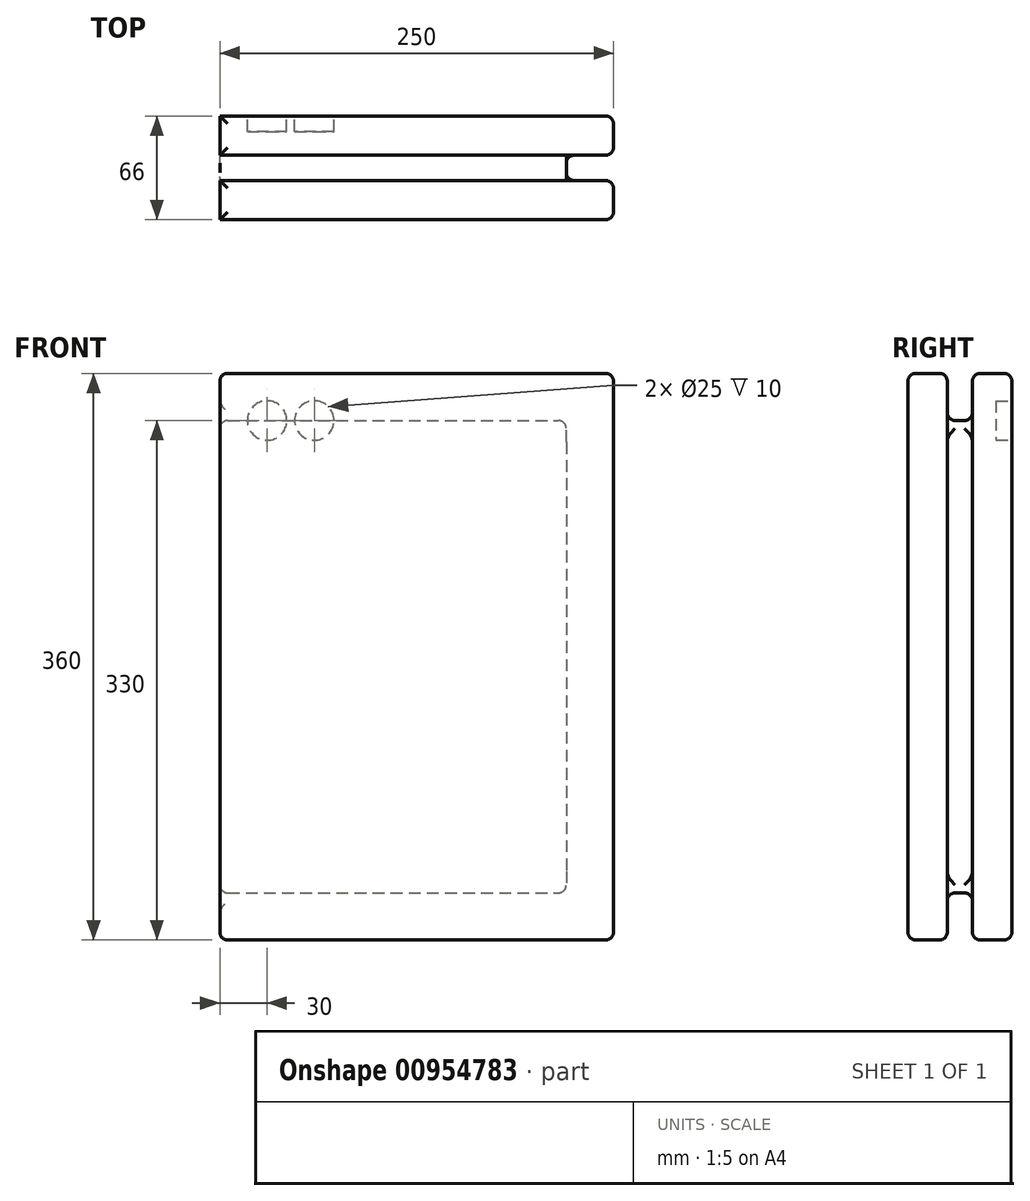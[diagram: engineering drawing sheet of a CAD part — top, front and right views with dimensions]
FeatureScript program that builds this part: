
annotation { "Feature Type Name" : "Feature", "Feature Type Description" : "" }
export const myFeature = defineFeature(function(context is Context, id is Id, definition is map)
    precondition{}
    {
        {
            var Q0;
            Q0=qCreatedBy(makeId("Right.planeOp"),FACE);
            var sketch = newSketch(context, id + "F0", { "sketchPlane" : qUnion([Q0])});
            skLineSegment(sketch, "E0", {"start": v(0, 0) * mm, "end": v(0, 150) * mm, "construction": true});
            skLineSegment(sketch, "E1", {"start": v(0, 0) * mm, "end": v(0, -150) * mm, "construction": true});
            skLineSegment(sketch, "E2", {"start": v(0, 150) * mm, "end": v(8, 150) * mm});
            skLineSegment(sketch, "E3", {"start": v(8, 150) * mm, "end": v(8, 180) * mm});
            skLineSegment(sketch, "E4", {"start": v(8, 180) * mm, "end": v(33, 180) * mm});
            skLineSegment(sketch, "E5", {"start": v(0, 0) * mm, "end": v(80, 0) * mm, "construction": true});
            skLineSegment(sketch, "E6", {"start": v(0, 0) * mm, "end": v(-80, 0) * mm, "construction": true});
            skLineSegment(sketch, "E7.MirrorCS", {"start": v(8, -180) * mm, "end": v(33, -180) * mm});
            skLineSegment(sketch, "E8.MirrorCS", {"start": v(8, -150) * mm, "end": v(8, -180) * mm});
            skLineSegment(sketch, "E9.MirrorCS", {"start": v(0, -150) * mm, "end": v(8, -150) * mm});
            skLineSegment(sketch, "E10", {"start": v(33, 180) * mm, "end": v(33, -180) * mm});
            skLineSegment(sketch, "E11", {"start": v(0, 150) * mm, "end": v(0, -150) * mm, "construction": true});
            skLineSegment(sketch, "E12.MirrorCS", {"start": v(0, 150) * mm, "end": v(-8, 150) * mm});
            skLineSegment(sketch, "E13.MirrorCS", {"start": v(-8, 150) * mm, "end": v(-8, 180) * mm});
            skLineSegment(sketch, "E14.MirrorCS", {"start": v(-8, 180) * mm, "end": v(-33, 180) * mm});
            skLineSegment(sketch, "E15.MirrorCS", {"start": v(-33, 180) * mm, "end": v(-33, -180) * mm});
            skLineSegment(sketch, "E16.MirrorCS", {"start": v(-8, -180) * mm, "end": v(-33, -180) * mm});
            skLineSegment(sketch, "E17.MirrorCS", {"start": v(-8, -150) * mm, "end": v(-8, -180) * mm});
            skLineSegment(sketch, "E18.MirrorCS", {"start": v(0, -150) * mm, "end": v(-8, -150) * mm});
            skSolve(sketch);
        }
        {
            var Q0;
            Q0=qCreatedBy(makeId("Front.planeOp"),FACE);
            var sketch = newSketch(context, id + "F1", { "sketchPlane" : qUnion([Q0])});
            skLineSegment(sketch, "E19", {"start": v(0, 0) * mm, "end": v(250, 0) * mm});
            skSolve(sketch);
        }
        {
            var Q0;
            Q0 = qSketchRegion(id + "F0", true);
            var Q1;
            Q1 = qConstructionFilter(qBodyType(qCreatedBy(id + "F1" ,EDGE), BodyType.WIRE), ConstructionObject.NO);
            sweep(context, id + "F2", {"profiles" : qUnion([Q0]), "path" : qUnion([Q1])});
        }
        {
            var Q0;
            Q0=makeQuery(id+"F2.opSweep","SWEPT_FACE",FACE,{"disambiguationData":[OSD([sQuery(id+"F0.wireOp",EDGE,"E10"),sQuery(id+"F1.wireOp",EDGE,"E19")])]});
            var sketch = newSketch(context, id + "F3", { "sketchPlane" : qUnion([Q0])});
            skLineSegment(sketch, "E20", {"start": v(0, 180) * mm, "end": v(-30, 180) * mm, "construction": true});
            skLineSegment(sketch, "E21", {"start": v(-30, 180) * mm, "end": v(-60, 180) * mm, "construction": true});
            skLineSegment(sketch, "E22", {"start": v(-30, 180) * mm, "end": v(-30, 150) * mm, "construction": true});
            skLineSegment(sketch, "E23", {"start": v(-60, 180) * mm, "end": v(-60, 150) * mm, "construction": true});
            skCircle(sketch, "E24", {"center": v(-30, 150) * mm, "radius": 12.5 * mm});
            skCircle(sketch, "E25", {"center": v(-60, 150) * mm, "radius": 12.5 * mm});
            skSolve(sketch);
        }
        {
            var Q0;
            Q0=makeQuery(id+"F3.imprint","IMPRINT",FACE,{"disambiguationData":[TD([[makeQuery(id+"F3.imprint","IMPRINT",EDGE,{"derivedFrom":sQuery(id+"F3.wireOp",EDGE,"E25")}),1.0]])]});
            var Q1;
            Q1=makeQuery(id+"F3.imprint","IMPRINT",FACE,{"disambiguationData":[TD([[makeQuery(id+"F3.imprint","IMPRINT",EDGE,{"derivedFrom":sQuery(id+"F3.wireOp",EDGE,"E24")}),1.0]])]});
            extrude(context, id + "F4", {"entities" : qUnion([Q0, Q1]), "operationType" : NewBodyOperationType.REMOVE, "oppositeDirection" : true, "depth" : 10 * mm, "offsetDistance" : 25 * mm});
        }
        {
            var Q0;
            Q0=makeQuery(id+"F2.opSweep","CAP_FACE",FACE,{"disambiguationData":[OSD([sQuery(id+"F0.wireOp",EDGE,"E2"),sQuery(id+"F0.wireOp",EDGE,"E3"),sQuery(id+"F0.wireOp",EDGE,"E4"),sQuery(id+"F0.wireOp",EDGE,"E7.MirrorCS"),sQuery(id+"F0.wireOp",EDGE,"E8.MirrorCS"),sQuery(id+"F0.wireOp",EDGE,"E9.MirrorCS"),sQuery(id+"F0.wireOp",EDGE,"E10"),sQuery(id+"F0.wireOp",EDGE,"E12.MirrorCS"),sQuery(id+"F0.wireOp",EDGE,"E13.MirrorCS"),sQuery(id+"F0.wireOp",EDGE,"E14.MirrorCS"),sQuery(id+"F0.wireOp",EDGE,"E15.MirrorCS"),sQuery(id+"F0.wireOp",EDGE,"E16.MirrorCS"),sQuery(id+"F0.wireOp",EDGE,"E17.MirrorCS"),sQuery(id+"F0.wireOp",EDGE,"E18.MirrorCS"),sQuery(id+"F1.wireOp",VERTEX,"E19.end")])],"isStart":false});
            var sketch = newSketch(context, id + "F5", { "sketchPlane" : qUnion([Q0])});
            skPoint(sketch, "E26", {"position": v(0, 0) * mm});
            skLineSegment(sketch, "E27", {"start": v(0, 0) * mm, "end": v(0, 150) * mm, "construction": true});
            skLineSegment(sketch, "E28", {"start": v(0, 0) * mm, "end": v(0, -150) * mm, "construction": true});
            skLineSegment(sketch, "E29", {"start": v(0, 150) * mm, "end": v(-8, 150) * mm});
            skLineSegment(sketch, "E30", {"start": v(-8, 150) * mm, "end": v(-8, -150) * mm});
            skLineSegment(sketch, "E31", {"start": v(-8, -150) * mm, "end": v(0, -150) * mm});
            skLineSegment(sketch, "E32.MirrorCS", {"start": v(0, 150) * mm, "end": v(8, 150) * mm});
            skLineSegment(sketch, "E33.MirrorCS", {"start": v(8, 150) * mm, "end": v(8, -150) * mm});
            skLineSegment(sketch, "E34.MirrorCS", {"start": v(8, -150) * mm, "end": v(0, -150) * mm});
            skSolve(sketch);
        }
        {
            var Q0;
            Q0=makeQuery(id+"F5.imprint","IMPRINT",FACE,{"disambiguationData":[TD([[makeQuery(id+"F5.imprint","IMPRINT",EDGE,{"derivedFrom":sQuery(id+"F5.wireOp",EDGE,"E29")}),1.0]])]});
            extrude(context, id + "F6", {"entities" : qUnion([Q0]), "operationType" : NewBodyOperationType.REMOVE, "oppositeDirection" : true, "depth" : 30 * mm, "offsetDistance" : 25 * mm});
        }
        {
            var Q0;
            Q0=makeQuery(id+"F2.opSweep","SWEPT_FACE",FACE,{"disambiguationData":[OSD([sQuery(id+"F0.wireOp",EDGE,"E2"),sQuery(id+"F0.wireOp",EDGE,"E12.MirrorCS"),sQuery(id+"F1.wireOp",EDGE,"E19")])]});
            var Q1;
            Q1=makeQuery(id+"F2.opSweep","SWEPT_FACE",FACE,{"disambiguationData":[OSD([sQuery(id+"F0.wireOp",EDGE,"E9.MirrorCS"),sQuery(id+"F0.wireOp",EDGE,"E18.MirrorCS"),sQuery(id+"F1.wireOp",EDGE,"E19")])]});
            var Q2;
            Q2=makeQuery(id+"F2.opSweep","SWEPT_FACE",FACE,{"disambiguationData":[OSD([sQuery(id+"F0.wireOp",EDGE,"E7.MirrorCS"),sQuery(id+"F1.wireOp",EDGE,"E19")])]});
            var Q3;
            {var subQ1=sQuery(id+"F0.wireOp",EDGE,"E8.MirrorCS");var subQ2=sQuery(id+"F0.wireOp",EDGE,"E7.MirrorCS");var subQ3=sQuery(id+"F0.wireOp",EDGE,"E4");var subQ4=sQuery(id+"F0.wireOp",EDGE,"E3");var subQ5=sQuery(id+"F0.wireOp",EDGE,"E10");Q3=makeQuery(id+"F6.boolean.opBoolean","SPLIT",FACE,{"disambiguationData":[TD([makeQuery(id+"F6.opExtrude","SWEPT_FACE",FACE,{"disambiguationData":[OSD([sQuery(id+"F5.wireOp",EDGE,"E33.MirrorCS")])]})])],"derivedFrom":makeQuery(id+"F2.opSweep","CAP_FACE",FACE,{"disambiguationData":[OSD([sQuery(id+"F0.wireOp",EDGE,"E2"),subQ4,subQ3,subQ2,subQ1,sQuery(id+"F0.wireOp",EDGE,"E9.MirrorCS"),subQ5,sQuery(id+"F0.wireOp",EDGE,"E12.MirrorCS"),sQuery(id+"F0.wireOp",EDGE,"E13.MirrorCS"),sQuery(id+"F0.wireOp",EDGE,"E14.MirrorCS"),sQuery(id+"F0.wireOp",EDGE,"E15.MirrorCS"),sQuery(id+"F0.wireOp",EDGE,"E16.MirrorCS"),sQuery(id+"F0.wireOp",EDGE,"E17.MirrorCS"),sQuery(id+"F0.wireOp",EDGE,"E18.MirrorCS"),sQuery(id+"F1.wireOp",VERTEX,"E19.end")])],"isStart":false})});}
            var Q4;
            Q4=makeQuery(id+"F2.opSweep","SWEPT_FACE",FACE,{"disambiguationData":[OSD([sQuery(id+"F0.wireOp",EDGE,"E4"),sQuery(id+"F1.wireOp",EDGE,"E19")])]});
            var Q5;
            Q5=makeQuery(id+"F2.opSweep","SWEPT_FACE",FACE,{"disambiguationData":[OSD([sQuery(id+"F0.wireOp",EDGE,"E14.MirrorCS"),sQuery(id+"F1.wireOp",EDGE,"E19")])]});
            var Q6;
            {var subQ1=sQuery(id+"F0.wireOp",EDGE,"E16.MirrorCS");var subQ2=sQuery(id+"F0.wireOp",EDGE,"E15.MirrorCS");var subQ3=sQuery(id+"F0.wireOp",EDGE,"E14.MirrorCS");var subQ4=sQuery(id+"F0.wireOp",EDGE,"E13.MirrorCS");var subQ5=sQuery(id+"F0.wireOp",EDGE,"E17.MirrorCS");Q6=makeQuery(id+"F6.boolean.opBoolean","SPLIT",FACE,{"disambiguationData":[TD([makeQuery(id+"F6.opExtrude","SWEPT_FACE",FACE,{"disambiguationData":[OSD([sQuery(id+"F5.wireOp",EDGE,"E30")])]})])],"derivedFrom":makeQuery(id+"F2.opSweep","CAP_FACE",FACE,{"disambiguationData":[OSD([sQuery(id+"F0.wireOp",EDGE,"E2"),sQuery(id+"F0.wireOp",EDGE,"E3"),sQuery(id+"F0.wireOp",EDGE,"E4"),sQuery(id+"F0.wireOp",EDGE,"E7.MirrorCS"),sQuery(id+"F0.wireOp",EDGE,"E8.MirrorCS"),sQuery(id+"F0.wireOp",EDGE,"E9.MirrorCS"),sQuery(id+"F0.wireOp",EDGE,"E10"),sQuery(id+"F0.wireOp",EDGE,"E12.MirrorCS"),subQ4,subQ3,subQ2,subQ1,subQ5,sQuery(id+"F0.wireOp",EDGE,"E18.MirrorCS"),sQuery(id+"F1.wireOp",VERTEX,"E19.end")])],"isStart":false})});}
            var Q7;
            Q7=makeQuery(id+"F2.opSweep","SWEPT_FACE",FACE,{"disambiguationData":[OSD([sQuery(id+"F0.wireOp",EDGE,"E16.MirrorCS"),sQuery(id+"F1.wireOp",EDGE,"E19")])]});
            fillet(context, id + "F7", {"entities" : qUnion([Q0, Q1, Q2, Q3, Q4, Q5, Q6, Q7]), "radius" : 5 * mm, "tangentPropagation" : true, "allowEdgeOverflow" : false});
        }
    });
